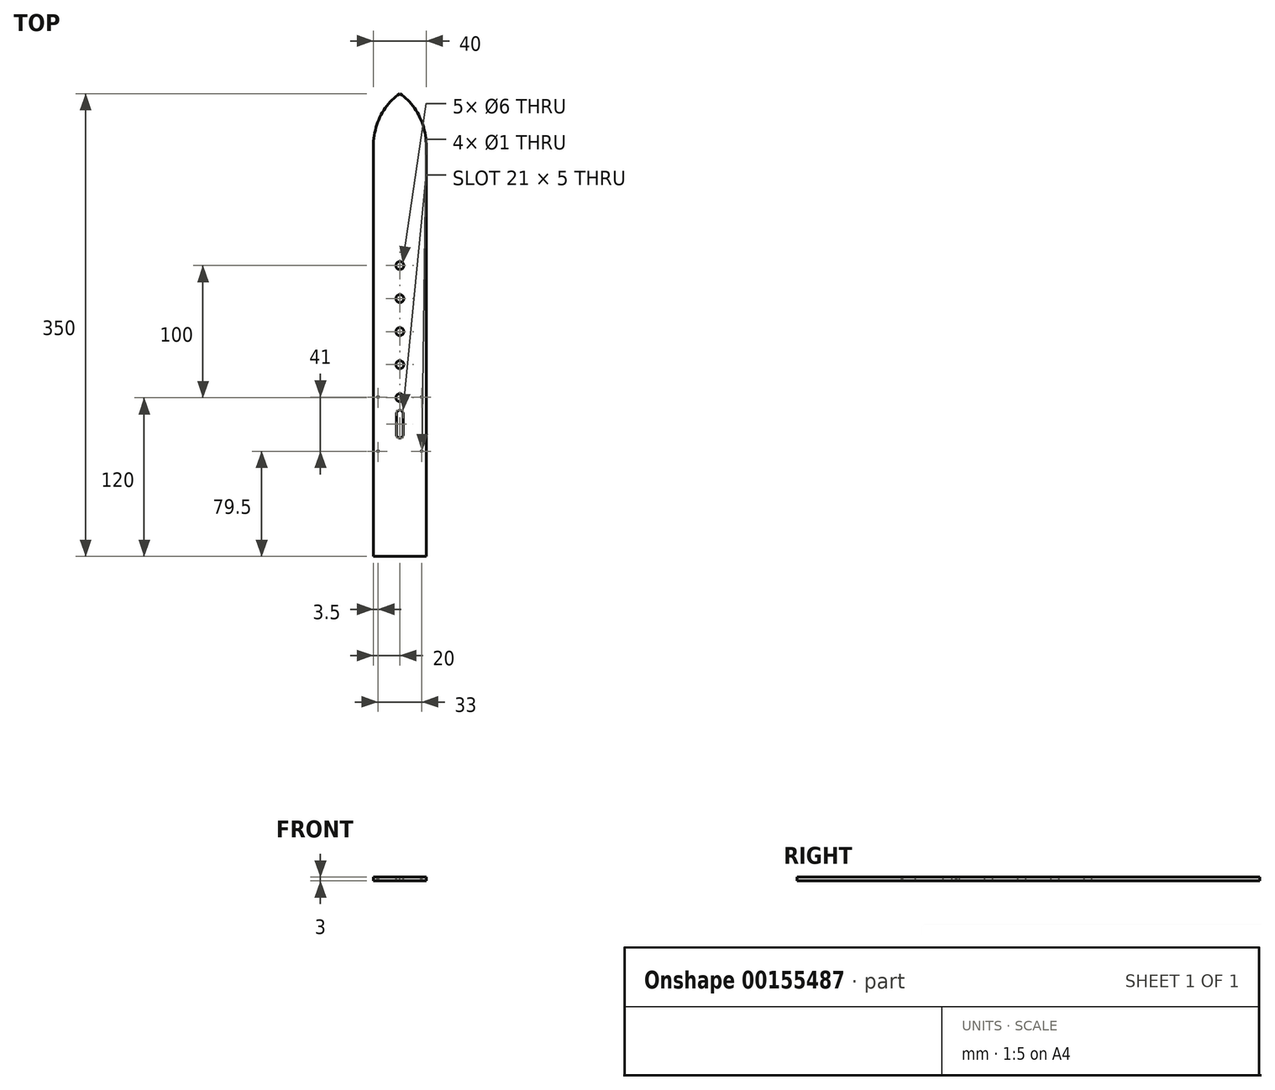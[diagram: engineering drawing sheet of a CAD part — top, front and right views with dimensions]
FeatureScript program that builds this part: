
annotation { "Feature Type Name" : "Feature", "Feature Type Description" : "" }
export const myFeature = defineFeature(function(context is Context, id is Id, definition is map)
    precondition{}
    {
        {
            var Q0;
            Q0=qCreatedBy(makeId("Top.planeOp"),FACE);
            var sketch = newSketch(context, id + "F0", { "sketchPlane" : qUnion([Q0])});
            skLineSegment(sketch, "E0.top", {"start": v(20, 0) * mm, "end": v(-20, 0) * mm});
            skLineSegment(sketch, "E0.left", {"start": v(20, 310) * mm, "end": v(20, 0) * mm});
            skLineSegment(sketch, "E0.right", {"start": v(-20, 310) * mm, "end": v(-20, 0) * mm});
            skEllipticalArc(sketch, "E1", {});
            skEllipticalArc(sketch, "E2", {});
            skLineSegment(sketch, "E3", {"start": v(0, 350) * mm, "end": v(0, 310) * mm, "construction": true});
            const initialGuessF0  = {"E1": [0.02, 0.31, -1, 0, 0.04, 0.0461880215351701, 5.23598775598299, 6.283185307179586], "E2": [-0.02, 0.31, 1, 0, 0.04, 0.0461880215351701, 6.283185307179586, 1.0471975511965956]};
            skSetInitialGuess(sketch, initialGuessF0);
            skSolve(sketch);
        }
        {
            var Q0;
            Q0 = qSketchRegion(id + "F0", true);
            extrude(context, id + "F1", {"entities" : qUnion([Q0]), "oppositeDirection" : true, "depth" : 3 * mm});
        }
        {
            var Q0;
            Q0=qCreatedBy(makeId("Top.planeOp"),FACE);
            var sketch = newSketch(context, id + "F2", { "sketchPlane" : qUnion([Q0])});
            skLineSegment(sketch, "E4.left", {"start": v(-2.5, 108) * mm, "end": v(-2.5, 92) * mm});
            skLineSegment(sketch, "E4.right", {"start": v(2.5, 108) * mm, "end": v(2.5, 92) * mm});
            skPoint(sketch, "E4.middle", {"position": v(0, 100) * mm});
            skArc(sketch, "E5", {"start": v(-2.5, 108) * mm, "mid": v(0, 110.5) * mm, "end": v(2.5, 108) * mm});
            skArc(sketch, "E6", {"start": v(2.5, 92) * mm, "mid": v(0, 89.5) * mm, "end": v(-2.5, 92) * mm});
            skSolve(sketch);
        }
        {
            var Q0;
            Q0 = qSketchRegion(id + "F2", true);
            extrude(context, id + "F3", {"entities" : qUnion([Q0]), "operationType" : NewBodyOperationType.REMOVE, "endBound" : BoundingType.THROUGH_ALL, "oppositeDirection" : true, "depth" : 3 * mm});
        }
        {
            var Q0;
            Q0=qCreatedBy(makeId("Top.planeOp"),FACE);
            var sketch = newSketch(context, id + "F4", { "sketchPlane" : qUnion([Q0])});
            skCircle(sketch, "E7", {"center": v(0, 220) * mm, "radius": 3 * mm});
            skCircle(sketch, "E8.0.1.0", {"center": v(0, 195) * mm, "radius": 3 * mm});
            skCircle(sketch, "E8.0.2.0", {"center": v(0, 170) * mm, "radius": 3 * mm});
            skCircle(sketch, "E8.0.3.0", {"center": v(0, 145) * mm, "radius": 3 * mm});
            skCircle(sketch, "E8.0.4.0", {"center": v(0, 120) * mm, "radius": 3 * mm});
            skLineSegment(sketch, "E8.direction1", {"start": v(0, 220) * mm, "end": v(25, 220) * mm, "construction": true});
            skLineSegment(sketch, "E8.direction2", {"start": v(0, 220) * mm, "end": v(0, 195) * mm, "construction": true});
            skSolve(sketch);
        }
        {
            var Q0;
            Q0 = qSketchRegion(id + "F4", true);
            extrude(context, id + "F5", {"entities" : qUnion([Q0]), "operationType" : NewBodyOperationType.REMOVE, "endBound" : BoundingType.THROUGH_ALL, "oppositeDirection" : true, "depth" : 25 * mm});
        }
        {
            var Q0;
            Q0=qCreatedBy(makeId("Top.planeOp"),FACE);
            var sketch = newSketch(context, id + "F6", { "sketchPlane" : qUnion([Q0])});
            skLineSegment(sketch, "E9.bottom", {"start": v(16.5, 120.5) * mm, "end": v(-16.5, 120.5) * mm, "construction": true});
            skLineSegment(sketch, "E9.top", {"start": v(16.5, 79.5) * mm, "end": v(-16.5, 79.5) * mm, "construction": true});
            skLineSegment(sketch, "E9.left", {"start": v(16.5, 120.5) * mm, "end": v(16.5, 79.5) * mm, "construction": true});
            skLineSegment(sketch, "E9.right", {"start": v(-16.5, 120.5) * mm, "end": v(-16.5, 79.5) * mm, "construction": true});
            skPoint(sketch, "E9.middle", {"position": v(0, 100) * mm});
            skLineSegment(sketch, "E10", {"start": v(0, 108) * mm, "end": v(0, 92) * mm, "construction": true});
            skCircle(sketch, "E11", {"center": v(-16.5, 120.5) * mm, "radius": 0.5 * mm});
            skCircle(sketch, "E12", {"center": v(16.5, 120.5) * mm, "radius": 0.5 * mm});
            skCircle(sketch, "E13", {"center": v(-16.5, 79.5) * mm, "radius": 0.5 * mm});
            skCircle(sketch, "E14", {"center": v(16.5, 79.5) * mm, "radius": 0.5 * mm});
            skSolve(sketch);
        }
        {
            var Q0;
            Q0 = qSketchRegion(id + "F6", true);
            extrude(context, id + "F7", {"entities" : qUnion([Q0]), "operationType" : NewBodyOperationType.REMOVE, "endBound" : BoundingType.THROUGH_ALL, "oppositeDirection" : true, "depth" : 25 * mm});
        }
    });
